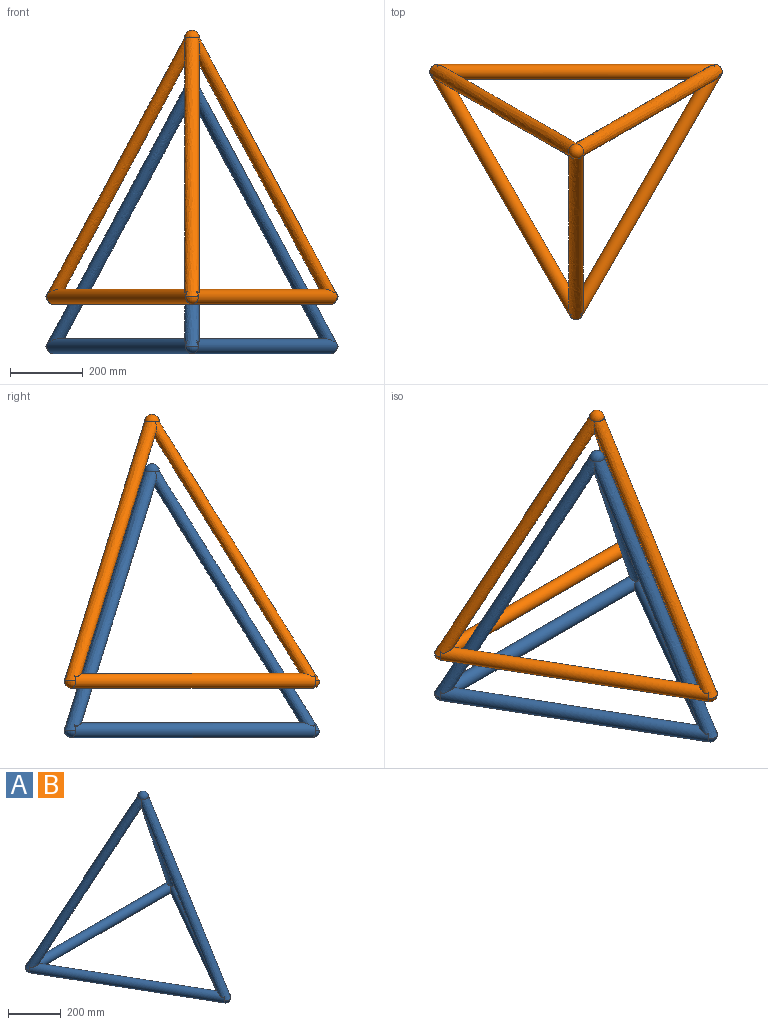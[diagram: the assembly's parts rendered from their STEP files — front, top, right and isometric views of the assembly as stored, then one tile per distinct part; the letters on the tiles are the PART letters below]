
ASSEMBLY  parts=2 mates=1
PART A: 34 faces, bbox 803x701x751.8 mm
  f0: plane 6.75x1.17mm, normal (0,0,-1), area 0.2mm2, adj f15,f32
  f1: plane 6.14x3.55mm, normal (0,0,-1), area 0.1mm2, adj f15,f32
  f2: plane 6.62x2.41mm, normal (0,0,-1), area 0.1mm2, adj f15,f32
  f3: plane 6.63x2.41mm, normal (0,0,-1), area 0.5mm2, adj f17,f29
  f4: plane 6.62x2.41mm, normal (0,0,-1), area 0.1mm2, adj f17,f29
  f5: plane 6.11x3.53mm, normal (0,0,-1), area 0.1mm2, adj f17,f29
  f6: plane 5.41x4.54mm, normal (0,0,-1), area 0.6mm2, adj f13,f26
  f7: plane 6.92x1.22mm, normal (0,0,-1), area 0mm2, adj f13,f26
  f8: plane 6.91x1.22mm, normal (0,0,-1), area 0mm2, adj f13,f26
  f9: plane 14.39x5.17mm, normal (0.5,0.87,0), area 12.5mm2, adj f11,f17
  f10: plane 14.39x5.17mm, normal (-0.5,-0.87,0), area 12.5mm2, adj f11,f13
  f11: cylinder r=20.32mm len=680.23mm, axis (-0.5,-0.87,0), area 93061.1mm2, adj f9,f10,f13,f17,f20,f23,f26,f29
  f12: plane 5.41x4.54mm, normal (0,0,-1), area 0.5mm2, adj f13,f26
  f13: bspline ~711.2x480.18mm, area 94922.5mm2, adj f6,f7,f8,f10,f11,f12,f15,f17
  f14: plane 6.63x2.41mm, normal (0,0,-1), area 0.6mm2, adj f15,f32
  f15: bspline ~711.2x421.54mm, area 94829.2mm2, adj f0,f1,f2,f13,f14,f17,f18,f20
  f16: plane 6.71x1.14mm, normal (0,0,-1), area 0.2mm2, adj f17,f29
  f17: bspline ~711.2x421.5mm, area 94947.8mm2, adj f3,f4,f5,f9,f11,f13,f15,f16
  f18: plane 14.39x5.97mm, normal (-1,0,0), area 12.5mm2, adj f15,f20
  f19: plane 14.39x5.97mm, normal (1,0,0), area 12.5mm2, adj f17,f20
  f20: cylinder r=20.32mm len=762mm, axis (1,0,0), area 93057.1mm2, adj f11,f15,f17,f18,f19,f23,f29,f32
  f21: plane 14.39x5.17mm, normal (0.5,-0.87,0), area 12.5mm2, adj f13,f23
  f22: plane 14.39x5.18mm, normal (-0.5,0.87,0), area 12.5mm2, adj f15,f23
  f23: cylinder r=20.32mm len=680.23mm, axis (-0.5,0.87,0), area 93053mm2, adj f11,f13,f15,f20,f21,f22,f26,f32
  f24: plane 6.11x3.53mm, normal (0,0,1), area 0.1mm2, adj f13,f26
  f25: plane 6.11x3.53mm, normal (0,0,1), area 0.1mm2, adj f13,f26
  f26: bspline ~35.2x20.74mm, area 863.8mm2, adj f6,f7,f8,f11,f12,f13,f23,f24
  f27: plane 7.06x0.36mm, normal (0,0,1), area 0.1mm2, adj f17,f29
  f28: plane 5.4x4.53mm, normal (0,0,1), area 0.1mm2, adj f17,f29
  f29: bspline ~30.48x20.52mm, area 863.9mm2, adj f3,f4,f5,f11,f16,f17,f20,f27
  f30: plane 5.43x4.56mm, normal (0,0,1), area 0.1mm2, adj f15,f32
  f31: plane 7.1x0.38mm, normal (0,0,1), area 0.1mm2, adj f15,f32
  f32: bspline ~30.48x20.52mm, area 863.9mm2, adj f0,f1,f2,f14,f15,f20,f23,f30
  f33: sphere r=20.32mm, area 2594.3mm2, adj f13,f15,f17
PART B: same geometry as A
PLACE A t=(432.06,747.05,212.92)mm
PLACE B t=(432.06,747.05,348.46)mm
MATE slider A.f17 <-> B.f15  axis (0,0,1) through (432.06,747.05,924.12)mm
